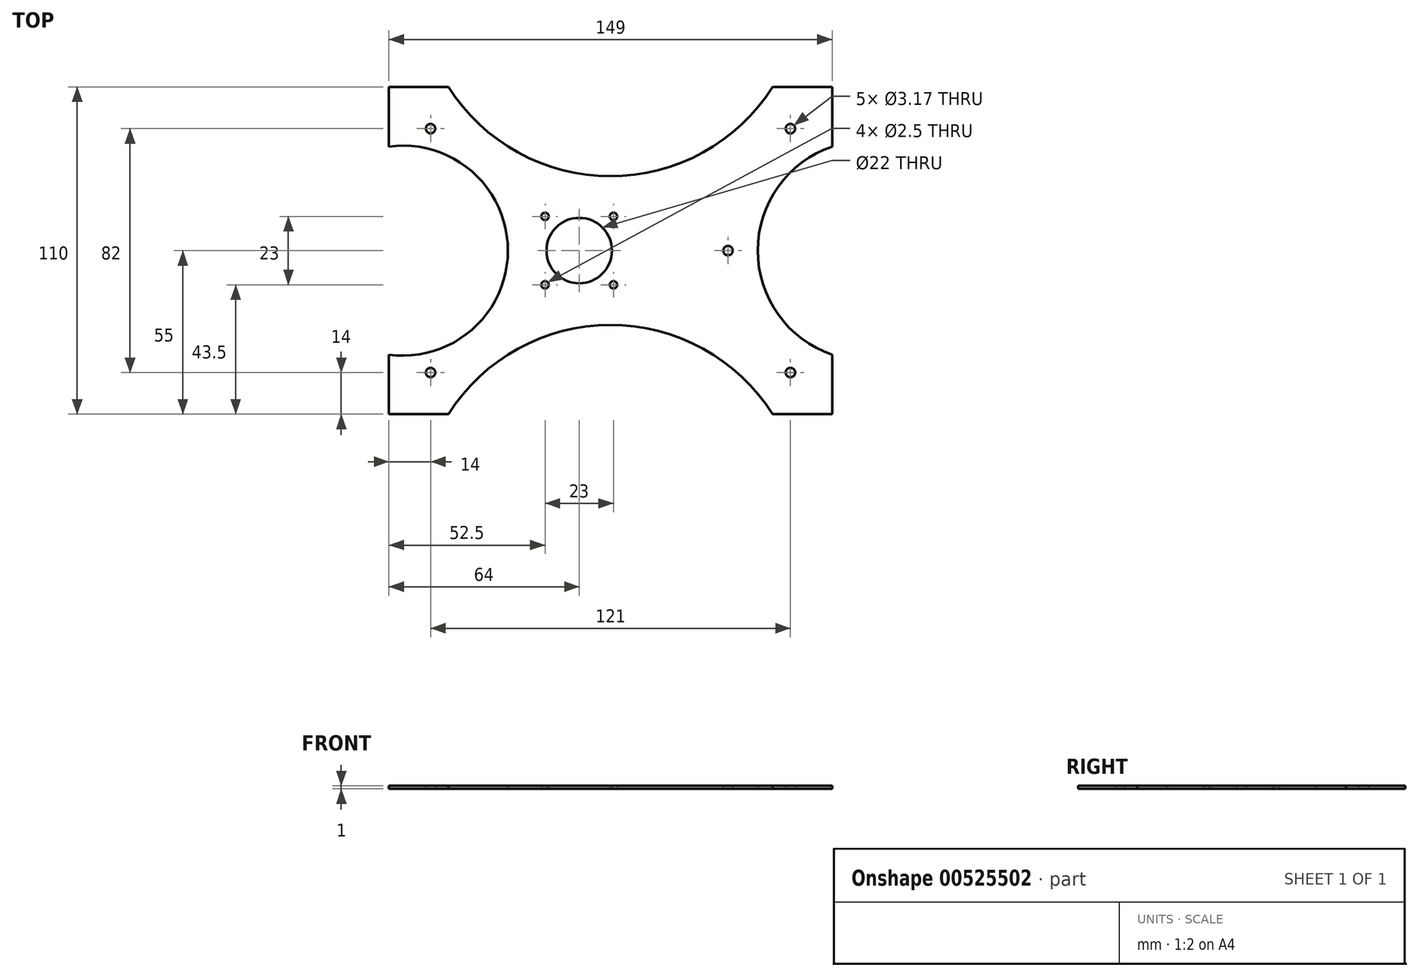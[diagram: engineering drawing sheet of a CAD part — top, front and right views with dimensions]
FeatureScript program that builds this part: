
annotation { "Feature Type Name" : "Feature", "Feature Type Description" : "" }
export const myFeature = defineFeature(function(context is Context, id is Id, definition is map)
    precondition{}
    {
        {
            var Q0;
            Q0=qCreatedBy(makeId("Top.planeOp"),FACE);
            var sketch = newSketch(context, id + "F0", { "sketchPlane" : qUnion([Q0])});
            skCircle(sketch, "E0", {"center": v(0, 0) * mm, "radius": 110 * mm});
            skCircle(sketch, "E1", {"center": v(0, 0) * mm, "radius": 11 * mm});
            skLineSegment(sketch, "E2.bottom", {"start": v(11.5, 11.5) * mm, "end": v(-11.5, 11.5) * mm, "construction": true});
            skLineSegment(sketch, "E2.top", {"start": v(11.5, -11.5) * mm, "end": v(-11.5, -11.5) * mm, "construction": true});
            skLineSegment(sketch, "E2.left", {"start": v(11.5, 11.5) * mm, "end": v(11.5, -11.5) * mm, "construction": true});
            skLineSegment(sketch, "E2.right", {"start": v(-11.5, 11.5) * mm, "end": v(-11.5, -11.5) * mm, "construction": true});
            skCircle(sketch, "E3", {"center": v(-11.5, 11.5) * mm, "radius": 1.25 * mm});
            skCircle(sketch, "E4", {"center": v(11.5, 11.5) * mm, "radius": 1.25 * mm});
            skCircle(sketch, "E5", {"center": v(11.5, -11.5) * mm, "radius": 1.25 * mm});
            skCircle(sketch, "E6", {"center": v(-11.5, -11.5) * mm, "radius": 1.25 * mm});
            skCircle(sketch, "E7", {"center": v(50, 0) * mm, "radius": 1.59 * mm});
            skSolve(sketch);
        }
        {
            var Q0;
            Q0 = qSketchRegion(id + "F0", true);
            extrude(context, id + "F1", {"entities" : qUnion([Q0]), "depth" : 1 * mm, "offsetDistance" : 25 * mm});
        }
        {
            var Q0;
            Q0=qCreatedBy(makeId("Top.planeOp"),FACE);
            var sketch = newSketch(context, id + "F2", { "sketchPlane" : qUnion([Q0])});
            skCircle(sketch, "E8.0", {"center": v(0, 0) * mm, "radius": 110 * mm});
            skLineSegment(sketch, "E9.bottom", {"start": v(75, 45) * mm, "end": v(-75, 45) * mm});
            skLineSegment(sketch, "E9.top", {"start": v(75, -45) * mm, "end": v(-75, -45) * mm});
            skLineSegment(sketch, "E9.left", {"start": v(75, 45) * mm, "end": v(75, -45) * mm});
            skLineSegment(sketch, "E9.right", {"start": v(-75, 45) * mm, "end": v(-75, -45) * mm});
            skSolve(sketch);
        }
        {
            var Q0;
            Q0 = qSketchRegion(id + "F2", true);
            extrude(context, id + "F3", {"entities" : qUnion([Q0]), "operationType" : NewBodyOperationType.REMOVE, "endBound" : BoundingType.THROUGH_ALL, "depth" : 25 * mm, "offsetDistance" : 25 * mm});
        }
        {
            var Q0;
            Q0=qCreatedBy(makeId("Top.planeOp"),FACE);
            var sketch = newSketch(context, id + "F4", { "sketchPlane" : qUnion([Q0])});
            skCircle(sketch, "E10", {"center": v(-50, 41) * mm, "radius": 1.59 * mm});
            skCircle(sketch, "E11", {"center": v(-50, -41) * mm, "radius": 1.59 * mm});
            skCircle(sketch, "E12", {"center": v(71, -41) * mm, "radius": 1.59 * mm});
            skCircle(sketch, "E13", {"center": v(71, 41) * mm, "radius": 1.59 * mm});
            skSolve(sketch);
        }
        {
            var Q0;
            Q0 = qSketchRegion(id + "F4", true);
            extrude(context, id + "F5", {"entities" : qUnion([Q0]), "operationType" : NewBodyOperationType.REMOVE, "endBound" : BoundingType.THROUGH_ALL, "depth" : 25 * mm, "offsetDistance" : 25 * mm});
        }
        {
            var Q0;
            Q0=qCreatedBy(makeId("Top.planeOp"),FACE);
            var sketch = newSketch(context, id + "F6", { "sketchPlane" : qUnion([Q0])});
            skLineSegment(sketch, "E14.0", {"start": v(-75, 45) * mm, "end": v(75, 45) * mm, "construction": true});
            skLineSegment(sketch, "E15.0", {"start": v(-75, -45) * mm, "end": v(-75, 45) * mm, "construction": true});
            skCircle(sketch, "E16.0", {"center": v(-50, 41) * mm, "radius": 1.59 * mm, "construction": true});
            skLineSegment(sketch, "E17.bottom", {"start": v(-75, 45) * mm, "end": v(-54, 45) * mm});
            skLineSegment(sketch, "E17.top", {"start": v(-75, -45) * mm, "end": v(-54, -45) * mm});
            skLineSegment(sketch, "E17.left", {"start": v(-75, 45) * mm, "end": v(-75, -45) * mm});
            skLineSegment(sketch, "E17.right", {"start": v(-54, 45) * mm, "end": v(-54, -45) * mm});
            skSolve(sketch);
        }
        {
            var Q0;
            Q0 = qSketchRegion(id + "F6", true);
            extrude(context, id + "F7", {"entities" : qUnion([Q0]), "operationType" : NewBodyOperationType.REMOVE, "endBound" : BoundingType.THROUGH_ALL, "depth" : 25 * mm, "offsetDistance" : 25 * mm});
        }
        {
            var Q0;
            Q0=qCreatedBy(makeId("Top.planeOp"),FACE);
            var sketch = newSketch(context, id + "F8", { "sketchPlane" : qUnion([Q0])});
            skLineSegment(sketch, "E18.0", {"start": v(-54, -45) * mm, "end": v(-54, 45) * mm});
            skLineSegment(sketch, "E19.0", {"start": v(-54, 45) * mm, "end": v(75, 45) * mm});
            skLineSegment(sketch, "E20.0", {"start": v(-54, -45) * mm, "end": v(75, -45) * mm});
            skLineSegment(sketch, "E21.0", {"start": v(75, -45) * mm, "end": v(75, 45) * mm});
            skLineSegment(sketch, "E22.bottom", {"start": v(-64, 55) * mm, "end": v(85, 55) * mm});
            skLineSegment(sketch, "E22.top", {"start": v(-64, -55) * mm, "end": v(85, -55) * mm});
            skLineSegment(sketch, "E22.left", {"start": v(-64, 55) * mm, "end": v(-64, -55) * mm});
            skLineSegment(sketch, "E22.right", {"start": v(85, 55) * mm, "end": v(85, -55) * mm});
            skSolve(sketch);
        }
        {
            var Q0;
            Q0 = qSketchRegion(id + "F8", true);
            var Q1;
            Q1=makeQuery(id+"F1.opExtrude","CAP_FACE",FACE,{"disambiguationData":[OSD([sQuery(id+"F0.wireOp",EDGE,"E0"),sQuery(id+"F0.wireOp",EDGE,"E1"),sQuery(id+"F0.wireOp",EDGE,"E3"),sQuery(id+"F0.wireOp",EDGE,"E4"),sQuery(id+"F0.wireOp",EDGE,"E5"),sQuery(id+"F0.wireOp",EDGE,"E6"),sQuery(id+"F0.wireOp",EDGE,"E7")])],"isStart":false});
            extrude(context, id + "F9", {"entities" : qUnion([Q0]), "operationType" : NewBodyOperationType.ADD, "endBound" : BoundingType.UP_TO_SURFACE, "depth" : 25 * mm, "endBoundEntityFace" : qUnion([Q1]), "offsetDistance" : 25 * mm});
        }
        {
            var Q0;
            Q0=qCreatedBy(makeId("Top.planeOp"),FACE);
            var sketch = newSketch(context, id + "F10", { "sketchPlane" : qUnion([Q0])});
            skLineSegment(sketch, "E23.0", {"start": v(-44, 55) * mm, "end": v(65, 55) * mm});
            skLineSegment(sketch, "E24.0", {"start": v(-64, 35) * mm, "end": v(-64, -35) * mm});
            skLineSegment(sketch, "E25.0", {"start": v(-44, -55) * mm, "end": v(65, -55) * mm});
            skLineSegment(sketch, "E26.0", {"start": v(85, 35) * mm, "end": v(85, -35) * mm});
            skArc(sketch, "E27", {"start": v(-44, 55) * mm, "mid": v(10.5, 25) * mm, "end": v(65, 55) * mm});
            skArc(sketch, "E28", {"start": v(85, 35) * mm, "mid": v(60, 0) * mm, "end": v(85, -35) * mm});
            skArc(sketch, "E29", {"start": v(65, -55) * mm, "mid": v(10.5, -25) * mm, "end": v(-44, -55) * mm});
            skArc(sketch, "E30", {"start": v(-64, -35) * mm, "mid": v(-24, 0) * mm, "end": v(-64, 35) * mm});
            skPoint(sketch, "E31.orphan", {"position": v(-64, 55) * mm});
            skPoint(sketch, "E32.orphan", {"position": v(-64, -55) * mm});
            skPoint(sketch, "E33.orphan", {"position": v(85, -55) * mm});
            skPoint(sketch, "E34.orphan", {"position": v(85, 55) * mm});
            skSolve(sketch);
        }
        {
            var Q0;
            Q0 = qSketchRegion(id + "F10", true);
            extrude(context, id + "F11", {"entities" : qUnion([Q0]), "operationType" : NewBodyOperationType.REMOVE, "depth" : 25 * mm, "offsetDistance" : 25 * mm});
        }
    });
